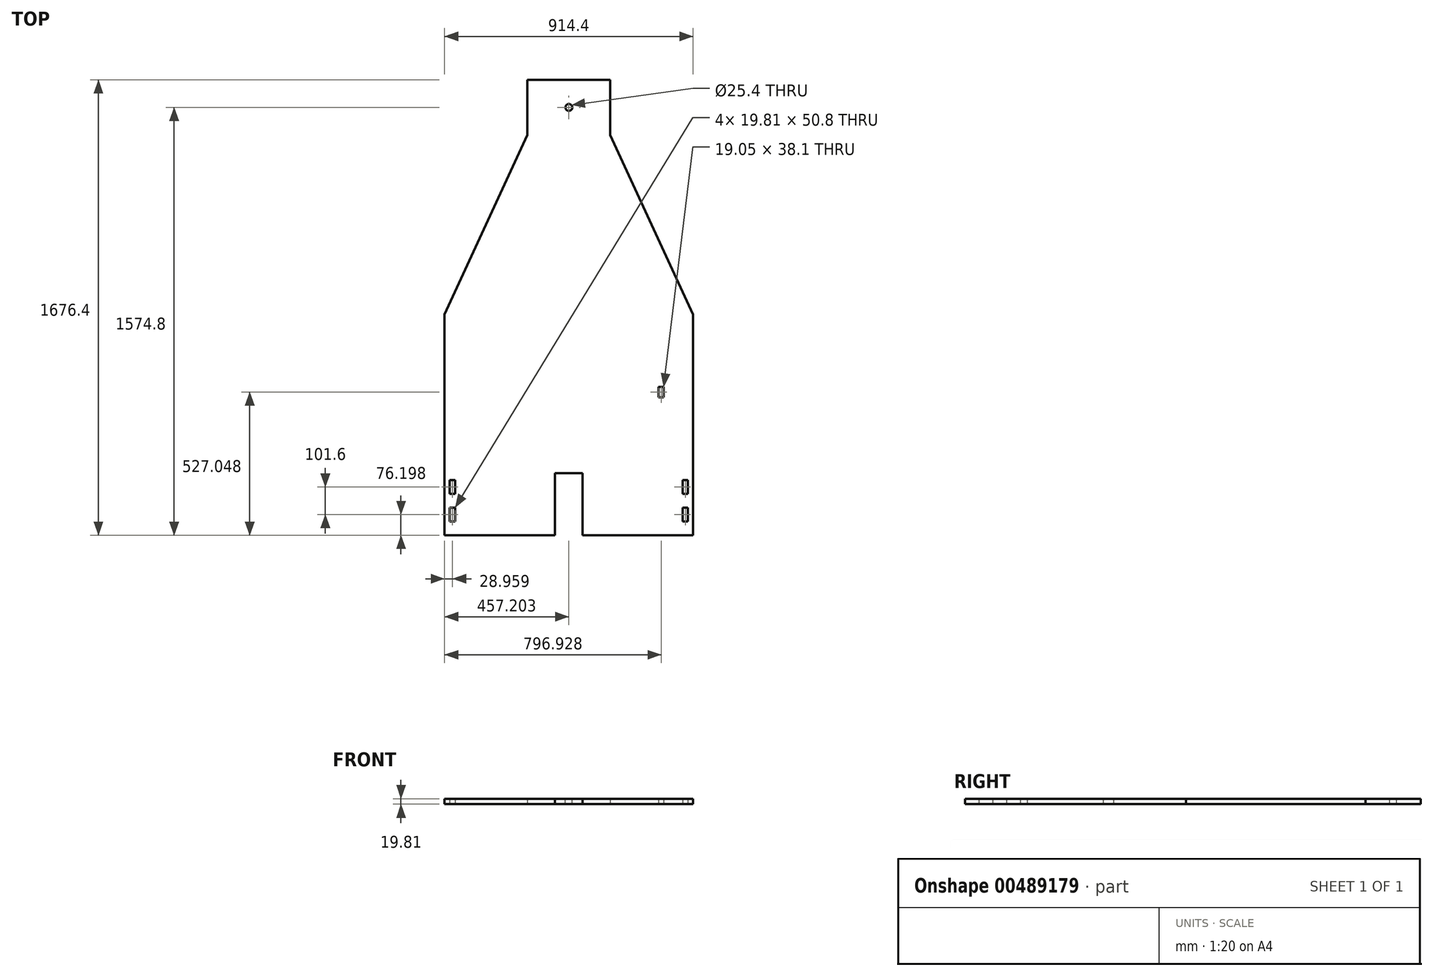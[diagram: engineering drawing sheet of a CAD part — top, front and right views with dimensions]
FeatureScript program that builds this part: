
annotation { "Feature Type Name" : "Feature", "Feature Type Description" : "" }
export const myFeature = defineFeature(function(context is Context, id is Id, definition is map)
    precondition{}
    {
        {
            var Q0;
            Q0=qCreatedBy(makeId("Top.planeOp"),FACE);
            var sketch = newSketch(context, id + "F0", { "sketchPlane" : qUnion([Q0])});
            skLineSegment(sketch, "E0", {"start": v(-468.3, -61.65) * mm, "end": v(446.1, -61.65) * mm});
            skLineSegment(sketch, "E1", {"start": v(-11.1, -61.65) * mm, "end": v(-11.1, 1614.75) * mm, "construction": true});
            skLineSegment(sketch, "E2", {"start": v(-468.3, -61.65) * mm, "end": v(-468.3, 751.15) * mm});
            skLineSegment(sketch, "E3", {"start": v(446.1, -61.65) * mm, "end": v(446.1, 751.15) * mm});
            skLineSegment(sketch, "E4", {"start": v(-11.1, 1614.75) * mm, "end": v(141.3, 1614.75) * mm});
            skLineSegment(sketch, "E5", {"start": v(-11.1, 1614.75) * mm, "end": v(-163.5, 1614.75) * mm});
            skLineSegment(sketch, "E6", {"start": v(446.1, 141.55) * mm, "end": v(293.7, 141.55) * mm, "construction": true});
            skLineSegment(sketch, "E7", {"start": v(-163.5, 1614.75) * mm, "end": v(-163.5, 1411.55) * mm});
            skLineSegment(sketch, "E8", {"start": v(141.3, 1614.75) * mm, "end": v(141.3, 1411.55) * mm});
            skLineSegment(sketch, "E9", {"start": v(-468.3, 751.15) * mm, "end": v(-163.5, 1411.55) * mm});
            skLineSegment(sketch, "E10", {"start": v(141.3, 1411.55) * mm, "end": v(446.1, 751.15) * mm});
            skLineSegment(sketch, "E11", {"start": v(98.72, -61.65) * mm, "end": v(98.72, 192.35) * mm, "construction": true});
            skLineSegment(sketch, "E12", {"start": v(-468.3, 192.35) * mm, "end": v(446.1, 192.35) * mm, "construction": true});
            skLineSegment(sketch, "E13", {"start": v(446.1, 192.35) * mm, "end": v(446.1, 141.55) * mm, "construction": true});
            skLineSegment(sketch, "E14", {"start": v(446.1, -61.65) * mm, "end": v(446.1, -10.85) * mm, "construction": true});
            skLineSegment(sketch, "E15", {"start": v(446.1, 192.35) * mm, "end": v(427.05, 192.35) * mm, "construction": true});
            skLineSegment(sketch, "E16", {"start": v(427.05, 141.55) * mm, "end": v(407.24, 141.55) * mm});
            skLineSegment(sketch, "E17", {"start": v(407.24, 141.55) * mm, "end": v(407.24, 90.75) * mm});
            skLineSegment(sketch, "E18", {"start": v(407.24, 90.75) * mm, "end": v(427.05, 90.75) * mm});
            skLineSegment(sketch, "E19", {"start": v(427.05, 90.75) * mm, "end": v(427.05, 141.55) * mm});
            skLineSegment(sketch, "E20", {"start": v(446.1, -10.85) * mm, "end": v(427.05, -10.85) * mm, "construction": true});
            skLineSegment(sketch, "E21", {"start": v(427.05, -10.85) * mm, "end": v(427.05, 39.95) * mm});
            skLineSegment(sketch, "E22", {"start": v(427.05, 39.95) * mm, "end": v(407.24, 39.95) * mm});
            skLineSegment(sketch, "E23", {"start": v(407.24, 39.95) * mm, "end": v(407.24, -10.85) * mm});
            skLineSegment(sketch, "E24", {"start": v(407.24, -10.85) * mm, "end": v(427.05, -10.85) * mm});
            skLineSegment(sketch, "E25", {"start": v(-468.3, 160.26) * mm, "end": v(-449.25, 160.26) * mm, "construction": true});
            skLineSegment(sketch, "E26", {"start": v(-449.25, 141.55) * mm, "end": v(-429.44, 141.55) * mm});
            skLineSegment(sketch, "E27", {"start": v(-429.44, 141.55) * mm, "end": v(-429.44, 90.75) * mm});
            skLineSegment(sketch, "E28", {"start": v(-429.44, 90.75) * mm, "end": v(-449.25, 90.75) * mm});
            skLineSegment(sketch, "E29", {"start": v(-449.25, 90.75) * mm, "end": v(-449.25, 141.55) * mm});
            skLineSegment(sketch, "E30", {"start": v(-449.25, 39.95) * mm, "end": v(-449.25, -10.85) * mm});
            skPoint(sketch, "E30.startSnap0", {"position": v(-315.9, 39.95) * mm});
            skLineSegment(sketch, "E31", {"start": v(-449.25, -10.85) * mm, "end": v(-429.44, -10.85) * mm});
            skLineSegment(sketch, "E32", {"start": v(-429.44, -10.85) * mm, "end": v(-429.44, 39.95) * mm});
            skLineSegment(sketch, "E33", {"start": v(-429.44, 39.95) * mm, "end": v(-449.25, 39.95) * mm});
            skLineSegment(sketch, "E34", {"start": v(319.1, 192.35) * mm, "end": v(319.1, 446.35) * mm, "construction": true});
            skLineSegment(sketch, "E35.bottom", {"start": v(319.1, 446.35) * mm, "end": v(338.15, 446.35) * mm});
            skLineSegment(sketch, "E35.top", {"start": v(319.1, 484.45) * mm, "end": v(338.15, 484.45) * mm});
            skLineSegment(sketch, "E35.left", {"start": v(319.1, 446.35) * mm, "end": v(319.1, 484.45) * mm});
            skLineSegment(sketch, "E35.right", {"start": v(338.15, 446.35) * mm, "end": v(338.15, 484.45) * mm});
            skLineSegment(sketch, "E36", {"start": v(-11.1, -61.65) * mm, "end": v(-61.9, -61.65) * mm});
            skLineSegment(sketch, "E37", {"start": v(-61.9, -61.65) * mm, "end": v(-61.9, 166.95) * mm});
            skLineSegment(sketch, "E38", {"start": v(-11.1, -61.65) * mm, "end": v(39.7, -61.65) * mm});
            skLineSegment(sketch, "E39", {"start": v(-61.9, 166.95) * mm, "end": v(39.7, 166.95) * mm});
            skLineSegment(sketch, "E40", {"start": v(39.7, 166.95) * mm, "end": v(39.7, -61.65) * mm});
            skLineSegment(sketch, "E41", {"start": v(338.15, 484.45) * mm, "end": v(338.15, 39.95) * mm, "construction": true});
            skLineSegment(sketch, "E42", {"start": v(-11.1, 166.95) * mm, "end": v(-11.1, -36.25) * mm, "construction": true});
            skLineSegment(sketch, "E43", {"start": v(-11.1, 166.95) * mm, "end": v(-11.1, 154.25) * mm, "construction": true});
            skLineSegment(sketch, "E44", {"start": v(319.1, 446.35) * mm, "end": v(319.1, 154.25) * mm, "construction": true});
            skLineSegment(sketch, "E45", {"start": v(319.1, 154.25) * mm, "end": v(-11.1, 154.25) * mm, "construction": true});
            skSolve(sketch);
        }
        {
            var Q0;
            {var subQ2=sQuery(id+"F0.wireOp",EDGE,"E2");Q0=makeQuery(id+"F0.imprint","IMPRINT",FACE,{"disambiguationData":[TD([[makeQuery(id+"F0.imprint","IMPRINT",EDGE,{"derivedFrom":subQ2}),-1.0]])]});}
            var Q1;
            {var subQ5=sQuery(id+"F0.wireOp",EDGE,"BCa3zfcT-LxVo-JwYt-mVp2-TDnGbHmZvkau");Q1=makeQuery(id+"F0.imprint","IMPRINT",FACE,{"disambiguationData":[TD([[makeQuery(id+"F0.imprint","IMPRINT",EDGE,{"derivedFrom":subQ5}),-1.0]])]});}
            var Q2;
            {var subQ5=sQuery(id+"F0.wireOp",EDGE,"Nz0vXvWb-8wGc-Evbo-syFk-l416oUO3yX9C");Q2=makeQuery(id+"F0.imprint","IMPRINT",FACE,{"disambiguationData":[TD([[makeQuery(id+"F0.imprint","IMPRINT",EDGE,{"derivedFrom":subQ5}),1.0]])]});}
            extrude(context, id + "F1", {"entities" : qUnion([Q0, Q1, Q2]), "depth" : 19.8 * mm, "offsetDistance" : 25.4 * mm});
        }
        {
            var Q0;
            Q0=makeQuery(id+"F1.opExtrude","CAP_FACE",FACE,{"disambiguationData":[OSD([sQuery(id+"F0.wireOp",EDGE,"E0"),sQuery(id+"F0.wireOp",EDGE,"E2"),sQuery(id+"F0.wireOp",EDGE,"E3"),sQuery(id+"F0.wireOp",EDGE,"E4"),sQuery(id+"F0.wireOp",EDGE,"E5"),sQuery(id+"F0.wireOp",EDGE,"FuIGFaZT-SbxG-byH8-RBC2-jmqawT2KOuiB"),sQuery(id+"F0.wireOp",EDGE,"80C8aYcW-2lyI-FiEv-t3vI-EisMGJIq4L8D")])],"isStart":false});
            var sketch = newSketch(context, id + "F2", { "sketchPlane" : qUnion([Q0])});
            skLineSegment(sketch, "E46", {"start": v(0, -61.65) * mm, "end": v(0, 141.55) * mm, "construction": true});
            skLineSegment(sketch, "E47.bottom", {"start": v(-163.5, 1614.75) * mm, "end": v(141.3, 1614.75) * mm});
            skLineSegment(sketch, "E47.top", {"start": v(-163.5, 1411.55) * mm, "end": v(141.3, 1411.55) * mm});
            skLineSegment(sketch, "E47.left", {"start": v(-163.5, 1614.75) * mm, "end": v(-163.5, 1411.55) * mm});
            skLineSegment(sketch, "E47.right", {"start": v(141.3, 1614.75) * mm, "end": v(141.3, 1411.55) * mm});
            skCircle(sketch, "E48", {"center": v(-11.1, 1513.15) * mm, "radius": 12.7 * mm});
            skPoint(sketch, "E48.centerSnap0", {"position": v(-11.1, 1411.55) * mm});
            skPoint(sketch, "E48.centerSnap1", {"position": v(-163.5, 1513.15) * mm});
            skSolve(sketch);
        }
        {
            var Q0;
            Q0=makeQuery(id+"F2.imprint","IMPRINT",FACE,{"disambiguationData":[TD([[makeQuery(id+"F2.imprint","IMPRINT",EDGE,{"derivedFrom":sQuery(id+"F2.wireOp",EDGE,"E48")}),1.0]])]});
            extrude(context, id + "F3", {"entities" : qUnion([Q0]), "operationType" : NewBodyOperationType.REMOVE, "oppositeDirection" : true, "depth" : 254 * mm, "offsetDistance" : 25.4 * mm});
        }
    });
